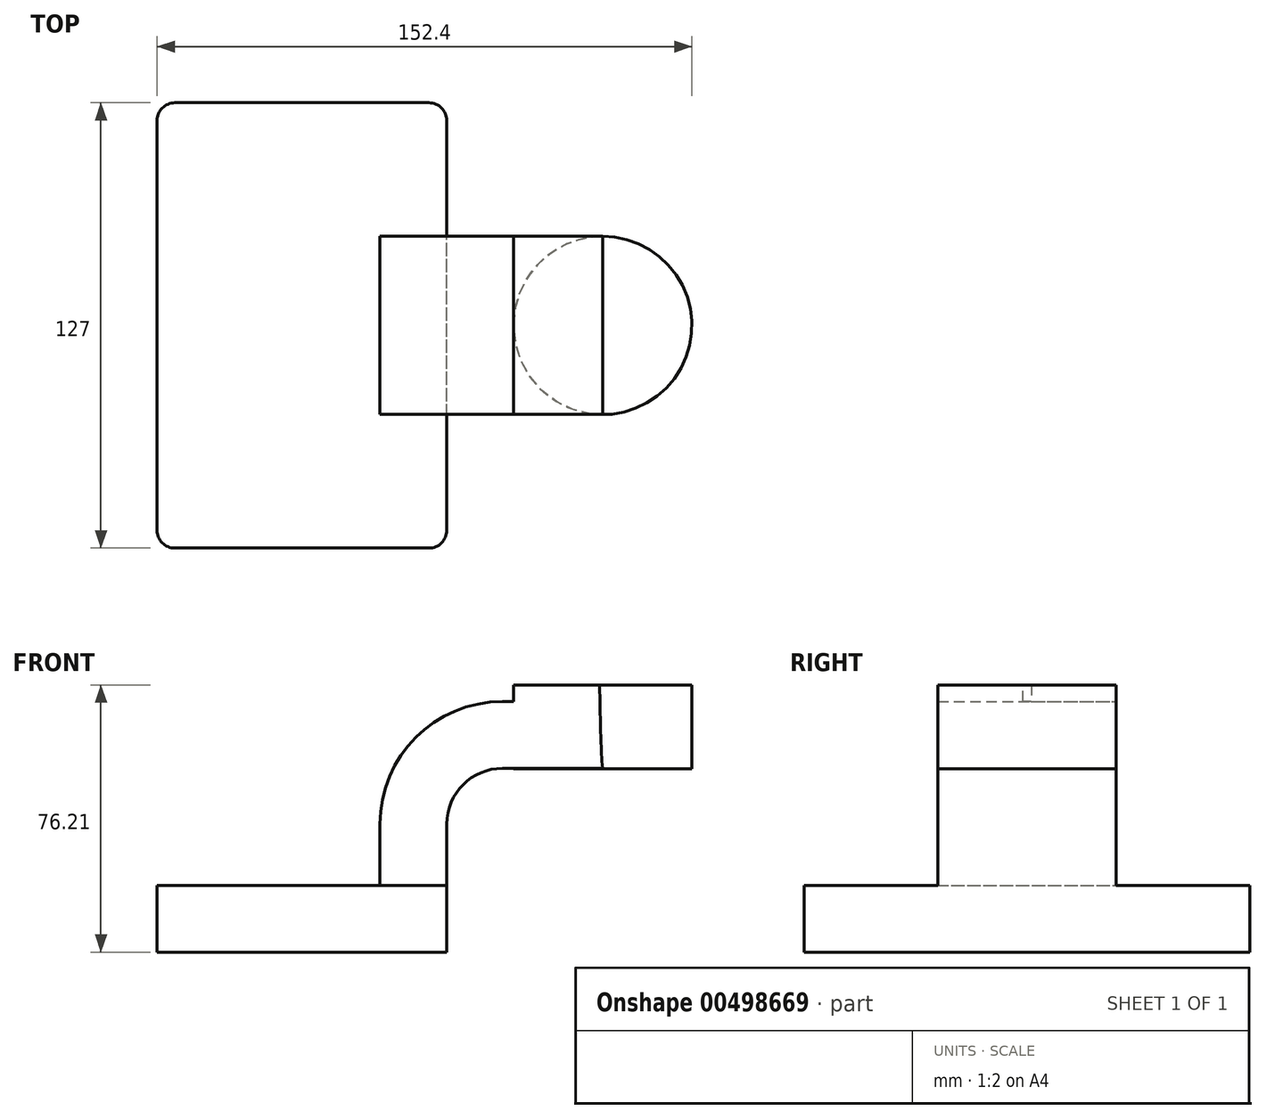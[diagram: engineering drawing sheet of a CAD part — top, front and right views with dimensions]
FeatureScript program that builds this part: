
annotation { "Feature Type Name" : "Feature", "Feature Type Description" : "" }
export const myFeature = defineFeature(function(context is Context, id is Id, definition is map)
    precondition{}
    {
        {
            var Q0;
            Q0=qCreatedBy(makeId("Front.planeOp"),FACE);
            var sketch = newSketch(context, id + "F0", { "sketchPlane" : qUnion([Q0])});
            skLineSegment(sketch, "E0.bottom", {"start": v(-41.28, -9.53) * mm, "end": v(41.28, -9.53) * mm});
            skLineSegment(sketch, "E0.top", {"start": v(-41.28, 9.53) * mm, "end": v(41.28, 9.53) * mm});
            skLineSegment(sketch, "E0.left", {"start": v(-41.28, -9.53) * mm, "end": v(-41.28, 9.53) * mm});
            skLineSegment(sketch, "E0.right", {"start": v(41.28, -9.53) * mm, "end": v(41.28, 9.53) * mm});
            skPoint(sketch, "E0.middle", {"position": v(0, 0) * mm});
            skLineSegment(sketch, "E1.bottom", {"start": v(60.33, 42.8) * mm, "end": v(111.13, 42.8) * mm});
            skLineSegment(sketch, "E1.top", {"start": v(60.33, 66.67) * mm, "end": v(111.13, 66.67) * mm});
            skLineSegment(sketch, "E1.left", {"start": v(60.33, 42.8) * mm, "end": v(60.33, 66.67) * mm});
            skLineSegment(sketch, "E1.right", {"start": v(111.13, 42.8) * mm, "end": v(111.13, 66.67) * mm});
            skPoint(sketch, "E1.middle", {"position": v(85.73, 54.74) * mm});
            skLineSegment(sketch, "E2", {"start": v(41.28, 9.52) * mm, "end": v(41.28, 27) * mm});
            skArc(sketch, "E3", {"start": v(41.27, 27) * mm, "mid": v(45.92, 38.23) * mm, "end": v(57.15, 42.88) * mm});
            skLineSegment(sketch, "E4", {"start": v(57.15, 42.88) * mm, "end": v(85.72, 42.88) * mm});
            skLineSegment(sketch, "E5.0", {"start": v(57.15, 61.93) * mm, "end": v(85.7, 61.93) * mm});
            skArc(sketch, "E5.1", {"start": v(22.22, 27) * mm, "mid": v(32.45, 51.7) * mm, "end": v(57.15, 61.93) * mm});
            skLineSegment(sketch, "E5.2", {"start": v(22.22, 9.52) * mm, "end": v(22.22, 27) * mm});
            skLineSegment(sketch, "E6", {"start": v(85.73, 42.8) * mm, "end": v(85.7, 66.67) * mm});
            skFitSpline(sketch, "E7", {"points": [v(-41.28, 9.53) * mm, v(60.33, 66.67) * mm], "startDerivative": vector(2.63, 130.86) * mm, "endDerivative": vector(128.74, 1.17) * mm});
            skSolve(sketch);
        }
        {
            var Q0;
            Q0=makeQuery(id+"F0.imprint","IMPRINT",FACE,{"disambiguationData":[TD([[makeQuery(id+"F0.imprint","IMPRINT",EDGE,{"derivedFrom":sQuery(id+"F0.wireOp",EDGE,"E0.bottom")}),1.0]])]});
            extrude(context, id + "F1", {"entities" : qUnion([Q0]), "endBound" : BoundingType.SYMMETRIC, "depth" : 127 * mm});
        }
        {
            var Q0;
            {var subQ1=sQuery(id+"F0.wireOp",EDGE,"E2");Q0=makeQuery(id+"F0.imprint","IMPRINT",FACE,{"disambiguationData":[TD([[makeQuery(id+"F0.imprint","IMPRINT",EDGE,{"derivedFrom":subQ1}),1.0]])]});}
            var Q1;
            {var subQ1=sQuery(id+"F0.wireOp",EDGE,"E4");var subQ3=sQuery(id+"F0.wireOp",EDGE,"E1.left");var subQ4=makeQuery(id+"F0.imprint","INTERSECT",VERTEX,{"derivedFrom":[subQ3,subQ1]});Q1=makeQuery(id+"F0.imprint","IMPRINT",FACE,{"disambiguationData":[TD([[makeQuery(id+"F0.imprint","IMPRINT",EDGE,{"disambiguationData":[TD([[subQ4,-1.0]])],"derivedFrom":subQ3}),-1.0]])]});}
            extrude(context, id + "F2", {"entities" : qUnion([Q0, Q1]), "operationType" : NewBodyOperationType.ADD, "endBound" : BoundingType.SYMMETRIC, "depth" : 50.8 * mm});
        }
        {
            var Q0;
            {var subQ0=sQuery(id+"F0.wireOp",EDGE,"E5.1");Q0=makeQuery(id+"F0.imprint","IMPRINT",FACE,{"disambiguationData":[TD([[makeQuery(id+"F0.imprint","IMPRINT",EDGE,{"derivedFrom":subQ0}),1.0]])]});}
            extrude(context, id + "F3", {"entities" : qUnion([Q0]), "operationType" : NewBodyOperationType.ADD, "endBound" : BoundingType.SYMMETRIC, "depth" : 15.88 * mm});
        }
        {
            var Q0;
            {var subQ4=sQuery(id+"F0.wireOp",EDGE,"E1.right");Q0=makeQuery(id+"F0.imprint","IMPRINT",FACE,{"disambiguationData":[TD([[makeQuery(id+"F0.imprint","IMPRINT",EDGE,{"derivedFrom":subQ4}),1.0]])]});}
            var Q1;
            Q1=sQuery(id+"F0.wireOp",EDGE,"E6");
            revolve(context, id + "F4", {"operationType" : NewBodyOperationType.ADD, "entities" : qUnion([Q0]), "axis" : qUnion([Q1]), "revolveType" : RevolveType.SYMMETRIC, "angle" : 180 * degree});
        }
        {
            var Q0;
            {var subQ4=sQuery(id+"F0.wireOp",EDGE,"E1.right");Q0=makeQuery(id+"F0.imprint","IMPRINT",FACE,{"disambiguationData":[TD([[makeQuery(id+"F0.imprint","IMPRINT",EDGE,{"derivedFrom":subQ4}),1.0]])]});}
            var Q1;
            Q1=sQuery(id+"F0.wireOp",EDGE,"E6");
            revolve(context, id + "F5", {"operationType" : NewBodyOperationType.ADD, "entities" : qUnion([Q0]), "axis" : qUnion([Q1]), "revolveType" : RevolveType.FULL});
        }
        {
            var Q0;
            Q0=makeQuery(id+"F1.opExtrude","CAP_EDGE",EDGE,{"disambiguationData":[OSD([sQuery(id+"F0.wireOp",EDGE,"E0.left")])],"isStart":false});
            var Q1;
            Q1=makeQuery(id+"F1.opExtrude","CAP_EDGE",EDGE,{"disambiguationData":[OSD([sQuery(id+"F0.wireOp",EDGE,"E0.right")])],"isStart":false});
            var Q2;
            Q2=makeQuery(id+"F1.opExtrude","CAP_EDGE",EDGE,{"disambiguationData":[OSD([sQuery(id+"F0.wireOp",EDGE,"E0.right")])],"isStart":true});
            var Q3;
            Q3=makeQuery(id+"F1.opExtrude","CAP_EDGE",EDGE,{"disambiguationData":[OSD([sQuery(id+"F0.wireOp",EDGE,"E0.left")])],"isStart":true});
            fillet(context, id + "F6", {"entities" : qUnion([Q0, Q1, Q2, Q3]), "radius" : 5.08 * mm, "tangentPropagation" : true, "allowEdgeOverflow" : false});
        }
    });
